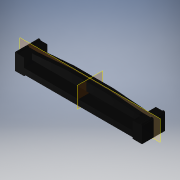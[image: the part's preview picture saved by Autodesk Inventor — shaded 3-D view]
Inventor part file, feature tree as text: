
AUTODESK INVENTOR PART (.ipt)
format: ipt  version: 2019 (Build 230136000, 136)  size: 237,568 bytes
history: native  units: mm (DEFAULTED — no unit token found)
features: sketch x8, extrude x5, fillet x1
ambient origin geometry x8: Origin, YZ Plane, XZ Plane, XY Plane, X Axis, Y Axis, Z Axis, Center Point
bodies: Solid1 (feature_tree)
feature tree (14):
  extrude  "Extrusion1"  Depth=10.0mm
  extrude  "Extrusion2"  Depth=47.0mm
  extrude  "Extrusion3"  Depth=7.4676mm TaperAngle=0.0deg
  extrude  "Extrusion4"  Depth=2.54mm
  extrude  "Extrusion5"  Depth=1.3208mm
  fillet  "Fillet1"  Radius=0.762mm
  sketch  "Sketch8"  dims[d15=8.128mm]
  sketch  "Sketch9"  dims[d16=16.891mm]
  sketch  "Sketch11"  dims[d17=0.508mm d18=3.302mm d19=0.0mm d20=1.143mm d21=3.302mm d22=0.0mm d23=0.5842mm d37=0.508mm d38=0.5842mm d39=0.254mm d40=160.0mm d42=1.27mm d43=10.0mm d45=25.4mm d48=1.27mm d49=1.27mm d50=1.27mm d51=1.27mm d53=1.27mm d54=1.27mm d55=1.27mm d56=1.27mm d57=1.27mm d58=1.27mm d59=1.27mm d60=1.27mm d61=1.27mm d62=1.27mm d64=0.4318mm d65=2.032mm d66=1.27mm d67=0.4318mm d68=0.4318mm d69=1.27mm d70=20.0mm d72=22.86mm d73=10.0mm d75=25.4mm d77=20.0mm d79=1.3843mm d80=10.0mm d82=25.4mm d84=20.0mm d86=1.016mm d87=10.0mm d89=25.4mm d91=20.0mm d93=1.016mm d94=10.0mm d96=25.4mm]
  sketch  "Sketch1"  dims[d0=55.0mm d1=10.0mm]
  sketch  "Sketch2"  dims[d2=7.4676mm d3=0.0mm d4=47.0mm]
  sketch  "Sketch3"  dims[d5=0.5842mm d6=7.4676mm d7=0.0mm]
  sketch  "Sketch4"  dims[d8=47.0mm d9=2.54mm]
  sketch  "Sketch5"  dims[d11=7.4676mm d12=0.0mm d13=1.3208mm d14=0.762mm]
